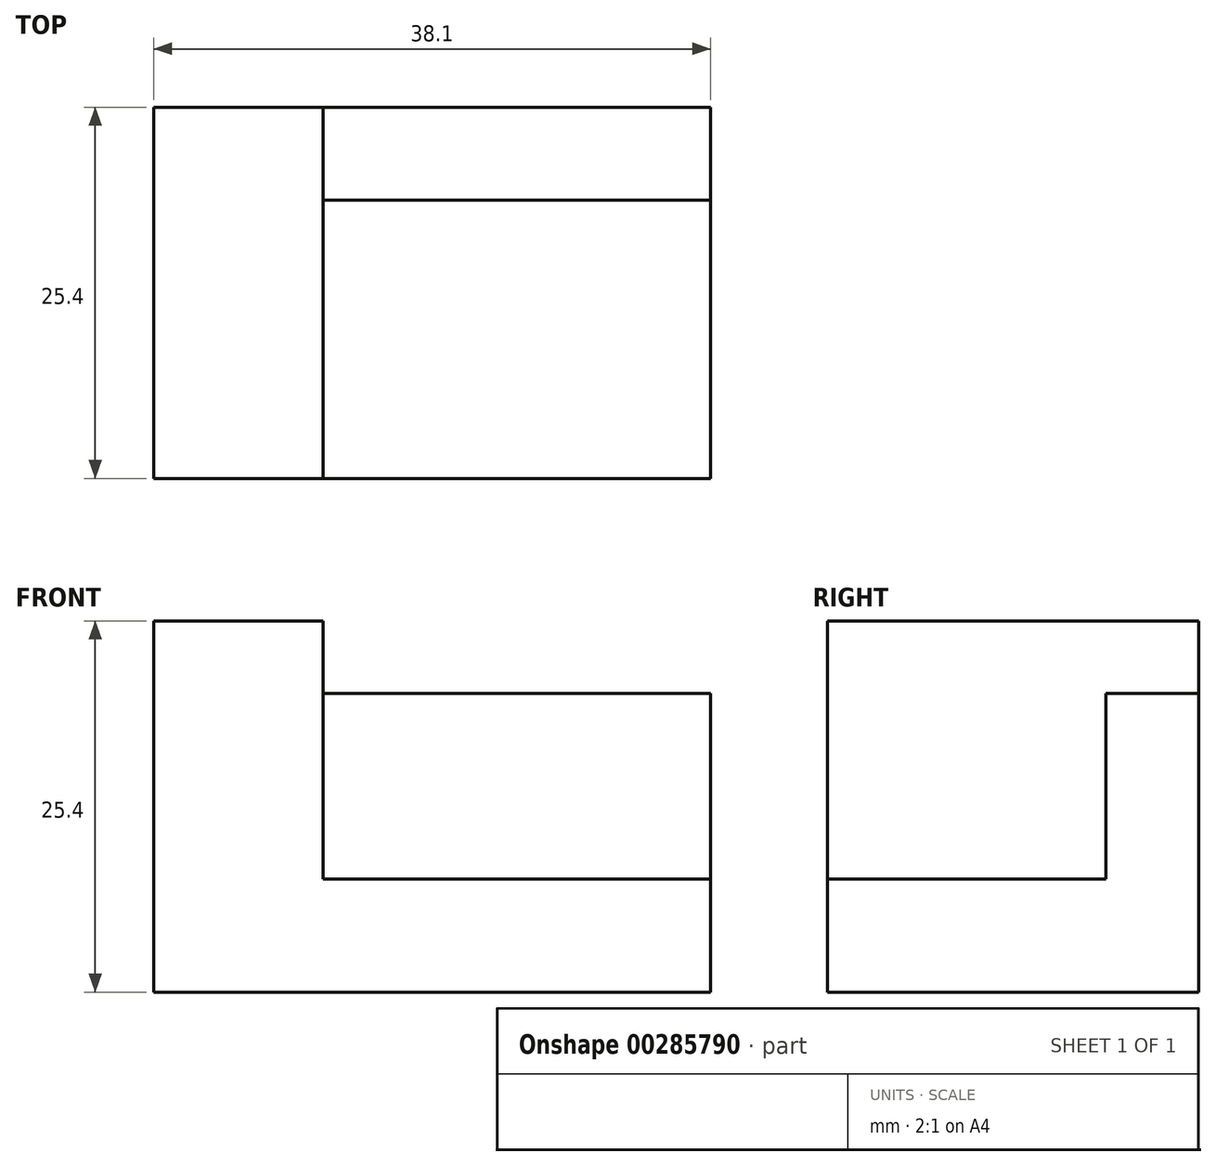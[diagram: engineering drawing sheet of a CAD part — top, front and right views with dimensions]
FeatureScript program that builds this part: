
annotation { "Feature Type Name" : "Feature", "Feature Type Description" : "" }
export const myFeature = defineFeature(function(context is Context, id is Id, definition is map)
    precondition{}
    {
        {
            var Q0;
            Q0=qCreatedBy(makeId("Front.planeOp"),FACE);
            var sketch = newSketch(context, id + "F0", { "sketchPlane" : qUnion([Q0])});
            skLineSegment(sketch, "E0", {"start": v(0, 0) * mm, "end": v(0, 25.4) * mm});
            skLineSegment(sketch, "E1", {"start": v(0, 25.4) * mm, "end": v(11.6, 25.4) * mm});
            skLineSegment(sketch, "E2", {"start": v(11.6, 25.4) * mm, "end": v(11.6, 7.73) * mm});
            skLineSegment(sketch, "E3", {"start": v(11.6, 7.73) * mm, "end": v(38.1, 7.73) * mm});
            skLineSegment(sketch, "E4", {"start": v(38.1, 7.73) * mm, "end": v(38.1, 0) * mm});
            skLineSegment(sketch, "E5", {"start": v(38.1, 0) * mm, "end": v(0, 0) * mm});
            skSolve(sketch);
        }
        {
            var Q0;
            Q0 = qSketchRegion(id + "F0", true);
            extrude(context, id + "F1", {"entities" : qUnion([Q0]), "depth" : 25.4 * mm});
        }
        {
            var Q0;
            Q0=makeQuery(id+"F1.opExtrude","SWEPT_FACE",FACE,{"disambiguationData":[OSD([sQuery(id+"F0.wireOp",EDGE,"E2")])]});
            var sketch = newSketch(context, id + "F2", { "sketchPlane" : qUnion([Q0])});
            skLineSegment(sketch, "E6.bottom", {"start": v(0, 7.73) * mm, "end": v(-6.35, 7.73) * mm});
            skLineSegment(sketch, "E6.top", {"start": v(0, 20.43) * mm, "end": v(-6.35, 20.43) * mm});
            skLineSegment(sketch, "E6.left", {"start": v(0, 7.73) * mm, "end": v(0, 20.43) * mm});
            skLineSegment(sketch, "E6.right", {"start": v(-6.35, 7.73) * mm, "end": v(-6.35, 20.43) * mm});
            skSolve(sketch);
        }
        {
            var Q0;
            Q0 = qSketchRegion(id + "F2", true);
            var Q1;
            Q1=makeQuery(id+"F1.opExtrude","SWEPT_FACE",FACE,{"disambiguationData":[OSD([sQuery(id+"F0.wireOp",EDGE,"E4")])]});
            extrude(context, id + "F3", {"entities" : qUnion([Q0]), "operationType" : NewBodyOperationType.ADD, "endBound" : BoundingType.UP_TO_SURFACE, "endBoundEntityFace" : qUnion([Q1]), "depth" : 25.4 * mm});
        }
    });
